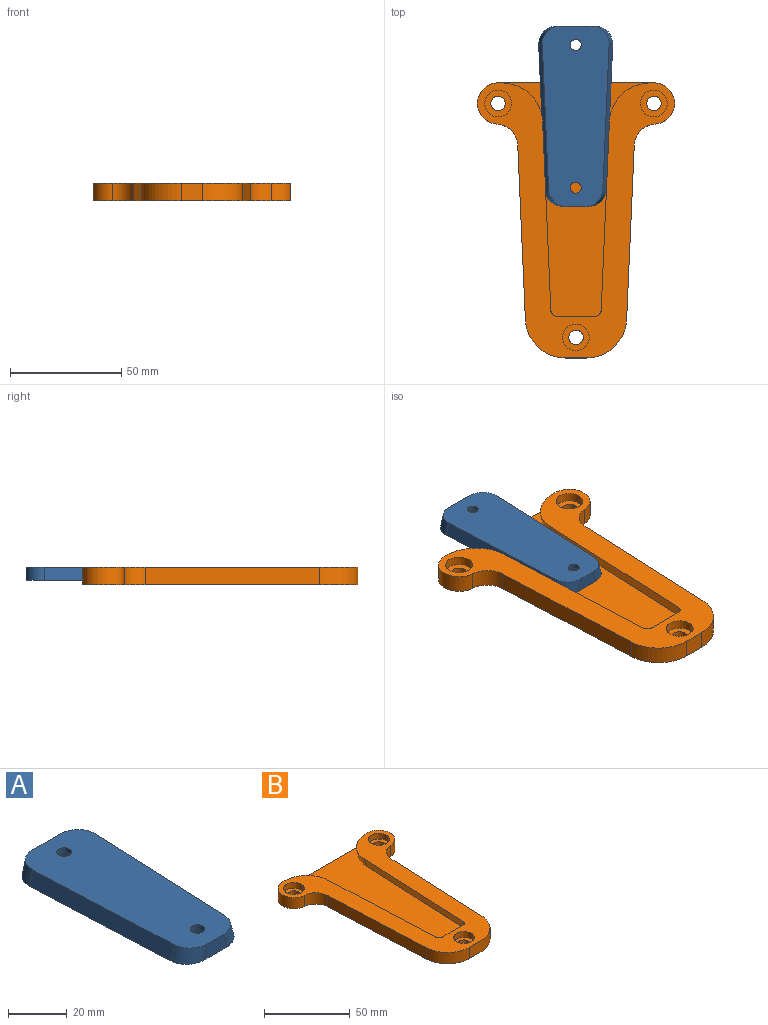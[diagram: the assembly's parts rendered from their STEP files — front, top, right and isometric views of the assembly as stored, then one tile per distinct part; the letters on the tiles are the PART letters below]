
ASSEMBLY  parts=2 mates=1
PART A: 16 faces, bbox 33.2x81.1x10.1 mm
  f0: cylinder r=2.5mm len=5mm, axis (0,0,1), area 31.4mm2, adj f3,f14
  f1: cylinder r=2.5mm len=5mm, axis (0,0,1), area 31.4mm2, adj f3,f12
  f2: plane 65.1x6mm, normal (0.97,-0.04,0.26), area 404.8mm2, adj f3,f4,f7,f8
  f3: plane 81.1x30.03mm, normal (0,0,1), area 2109.6mm2, adj f0,f1,f2,f5,f6,f7,f8,f9
  f4: plane 81.1x33.25mm, normal (0,0,-1), area 2252.8mm2, adj f2,f5,f6,f7,f8,f9,f10,f11
  f5: plane 16.68x6mm, normal (0,1,0), area 90.4mm2, adj f3,f4,f7,f10
  f6: plane 11x6mm, normal (0,-1,0), area 56.3mm2, adj f3,f4,f8,f11
  f7: cylinder r=8mm len=10.15mm, axis (0.26,0,-0.97), area 80.2mm2, adj f2,f3,f4,f5
  f8: cylinder r=8mm len=10.14mm, axis (-0.26,0,0.97), area 76mm2, adj f2,f3,f4,f6
  f9: plane 65.1x6mm, normal (-0.97,-0.04,0.26), area 404.8mm2, adj f3,f4,f10,f11
  f10: cylinder r=8mm len=10.15mm, axis (-0.26,0,-0.97), area 80.2mm2, adj f3,f4,f5,f9
  f11: cylinder r=8mm len=10.14mm, axis (0.26,0,0.97), area 76mm2, adj f3,f4,f6,f9
  f12: plane 10x10mm, normal (0,0,-1), area 58.9mm2, adj f1,f13
  f13: cylinder r=5mm len=10mm, axis (0,0,-1), area 125.7mm2, adj f4,f12
  f14: plane 10x10mm, normal (0,0,-1), area 58.9mm2, adj f0,f15
  f15: cylinder r=5mm len=10mm, axis (0,0,-1), area 125.7mm2, adj f4,f14
PART B: 31 faces, bbox 88.5x123.5x15.3 mm
  f0: cylinder r=3.25mm len=6.5mm, axis (0,0,1), area 81.7mm2, adj f8,f19
  f1: cylinder r=3.25mm len=6.5mm, axis (0,0,1), area 81.7mm2, adj f8,f16
  f2: plane 70x2mm, normal (0,1,0), area 140mm2, adj f7,f8,f11,f23
  f3: plane 5.15x1.38mm, normal (0,1,0), area 3.6mm2, adj f4,f7,f14
  f4: plane 123.5x88.5mm, normal (0,0,1), area 3280.6mm2, adj f3,f5,f6,f7,f9,f10,f12,f13
  f5: plane 9.49x8mm, normal (0,-1,0), area 75.9mm2, adj f4,f8,f15,f28
  f6: plane 78.26x8mm, normal (1,-0.04,0), area 626.6mm2, adj f4,f8,f9,f15
  f7: cylinder r=9.25mm len=18.48mm, axis (0,0,1), area 228.1mm2, adj f2,f3,f4,f8,f9,f11,f14
  f8: plane 123.5x88.5mm, normal (0,0,-1), area 6473.5mm2, adj f0,f1,f2,f5,f6,f7,f9,f15
  f9: cylinder r=10mm len=9.55mm, axis (0,0,1), area 117.4mm2, adj f4,f6,f7,f8
  f10: plane 84.88x6mm, normal (-0.97,0.04,-0.26), area 527.8mm2, adj f4,f11,f13,f14
  f11: plane 105x70.19mm, normal (0,0,1), area 3291.1mm2, adj f2,f7,f10,f12,f13,f14,f23,f25
  f12: plane 19.6x6mm, normal (0,1,0), area 107.9mm2, adj f4,f11,f13,f26
  f13: cylinder r=3mm len=7.55mm, axis (0.26,0,-0.97), area 28.5mm2, adj f4,f10,f11,f12
  f14: cylinder r=18mm len=20.22mm, axis (0.26,0,-0.97), area 170.9mm2, adj f3,f4,f7,f10,f11
  f15: cylinder r=18mm len=17.98mm, axis (0,0,1), area 219.9mm2, adj f4,f5,f6,f8
  f16: plane 12x12mm, normal (0,0,1), area 79.9mm2, adj f1,f17
  f17: cylinder r=6mm len=12mm, axis (0,0,1), area 150.8mm2, adj f4,f16
  f18: cylinder r=6mm len=12mm, axis (0,0,1), area 150.8mm2, adj f4,f19
  f19: plane 12x12mm, normal (0,0,1), area 79.9mm2, adj f0,f18
  f20: cylinder r=3.25mm len=6.5mm, axis (0,0,1), area 81.7mm2, adj f8,f29
  f21: plane 5.15x1.38mm, normal (0,1,0), area 3.6mm2, adj f4,f23,f27
  f22: plane 78.26x8mm, normal (-1,-0.04,0), area 626.6mm2, adj f4,f8,f24,f28
  f23: cylinder r=9.25mm len=18.48mm, axis (0,0,1), area 228.1mm2, adj f2,f4,f8,f11,f21,f24,f27
  f24: cylinder r=10mm len=9.55mm, axis (0,0,1), area 117.4mm2, adj f4,f8,f22,f23
  f25: plane 84.88x6mm, normal (0.97,0.04,-0.26), area 527.8mm2, adj f4,f11,f26,f27
  f26: cylinder r=3mm len=7.55mm, axis (-0.26,0,-0.97), area 28.5mm2, adj f4,f11,f12,f25
  f27: cylinder r=18mm len=20.22mm, axis (-0.26,0,-0.97), area 170.9mm2, adj f4,f11,f21,f23,f25
  f28: cylinder r=18mm len=17.98mm, axis (0,0,1), area 219.9mm2, adj f4,f5,f8,f22
  f29: plane 12x12mm, normal (0,0,1), area 79.9mm2, adj f20,f30
  f30: cylinder r=6mm len=12mm, axis (0,0,1), area 150.8mm2, adj f4,f29
PLACE A t=(7.86,51.81,15.07)mm
PLACE B t=(8,17.59,15.07)mm fixed
MATE planar A.f4 <-> B.f11  axis (0,0,-1) through (7.86,53.44,9.07)mm
